# Revit family: Cabinet-Teknion-CEKT_Cabinet_Kit_for_Two_Appliances_Doors-R2023
name_source: partatom
category: Furniture
units: mm (PartAtom-declared; Revit-internal decimal feet)

## family parameters
Always vertical = Yes
Cut with Voids When Loaded = No
Enable Cutting in Views = No
OmniClass Number = 23.40.20.00
OmniClass Title = General Furniture and Specialties
Render Appearance Source = Family Geometry
Room Calculation Point = No
Shared = Yes
Work Plane-Based = No

## types (7) — shared parameters
Assembly Code = E2020200
Manufacturer = Teknion
Manufacturer Fax = 416.661.4586
Part Number = CEKT
Product Documentation Link = https://www.teknion.com
Product Line = Storage Cabinets
Product Page URL = https://www.teknion.com
Series = Expansion Casework+
Sustainability Data = https://www.teknion.com
URL = www.teknion.com
Unit Weight URL = http://www.teknion.com
Warranty = http://www.teknion.com
zero-valued in all types: Default Elevation

## per-type parameters (varying)
| type | Adjustable Shelf | Appliance Section Height | Description | Height | Model |
| 96" H,75" Appliance Section Height | Yes | 75 " | Cabinet Kit for Two Appliances – Doors
,96" H,75" Appliance Section Height | 96 " | CEKT____9675 |
| 96" H,72" Appliance Section Height | Yes | 72 " | Cabinet Kit for Two Appliances – Doors
,96" H,72" Appliance Section Height | 96 " | CEKT____9672 |
| 96" H,69" Appliance Section Height | Yes | 69 " | Cabinet Kit for Two Appliances – Doors
,96" H,69" Appliance Section Height | 96 " | CEKT____9669 |
| 90" H,75" Appliance Section Height | No | 75 " | Cabinet Kit for Two Appliances – Doors
,90" H,75" Appliance Section Height | 90 " | CEKT____9075 |
| 90" H,72" Appliance Section Height | Yes | 72 " | Cabinet Kit for Two Appliances – Doors
,90" H,72" Appliance Section Height | 90 " | CEKT____9072 |
| 90" H,69" Appliance Section Height | Yes | 69 " | Cabinet Kit for Two Appliances – Doors
,90" H,69" Appliance Section Height | 90 " | CEKT____9069 |
| 84" H,69" Appliance Section Height | No | 69 " | Cabinet Kit for Two Appliances – Doors
,84" H,69" Appliance Section Height | 84 " | CEKT____8469 |

## geometry (parser evidence)
native form markers: Sweep x3
no freeform markers — native parametric forms only
